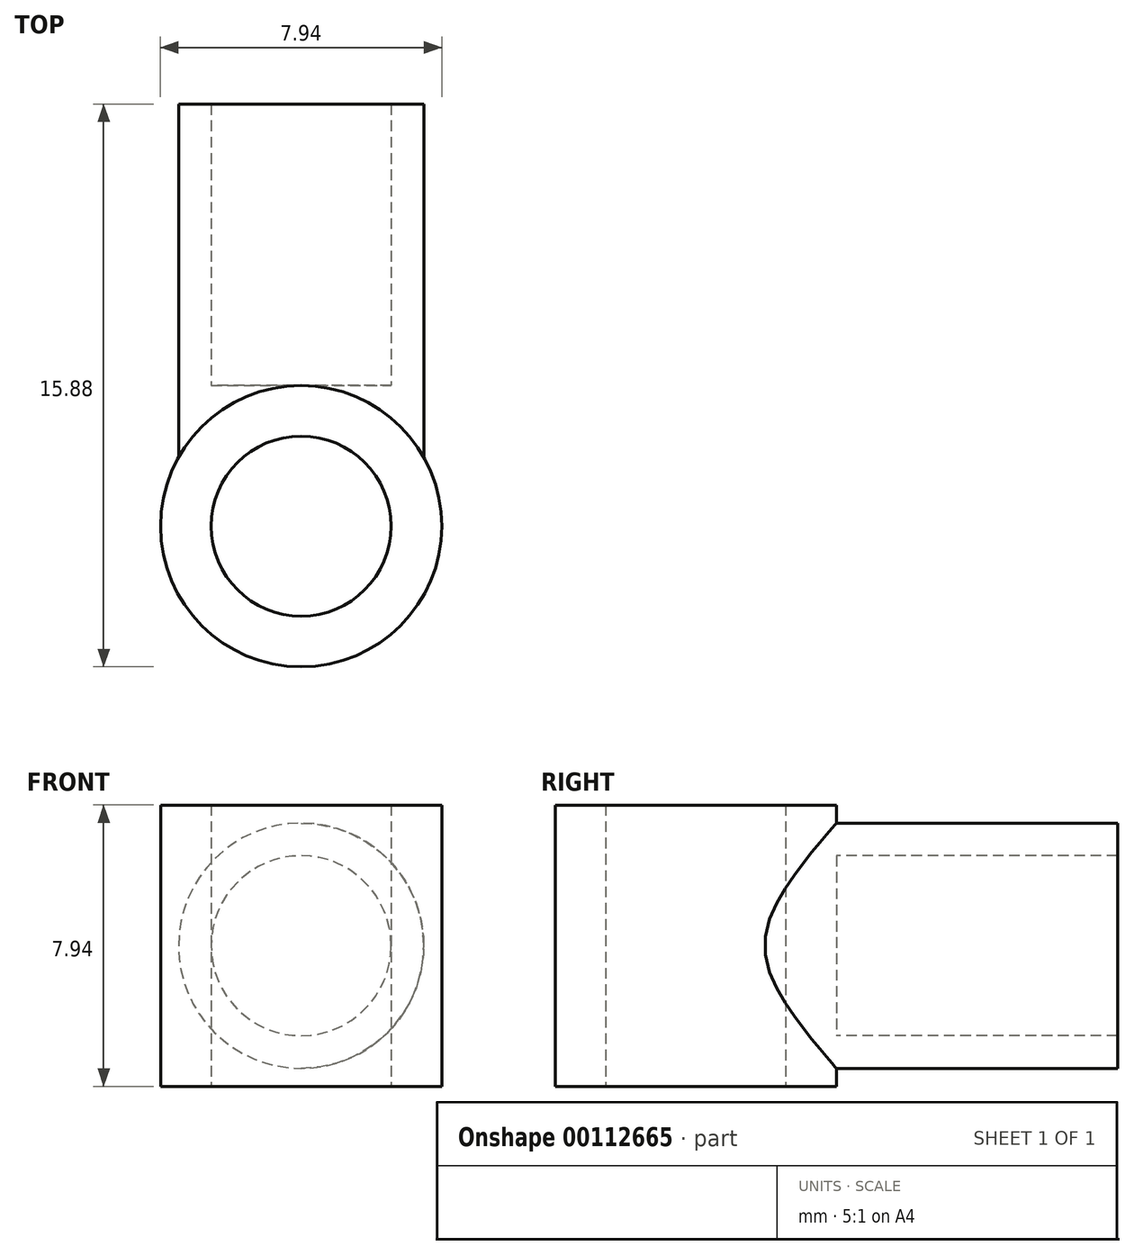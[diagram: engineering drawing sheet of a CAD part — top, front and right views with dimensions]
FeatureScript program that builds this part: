
annotation { "Feature Type Name" : "Feature", "Feature Type Description" : "" }
export const myFeature = defineFeature(function(context is Context, id is Id, definition is map)
    precondition{}
    {
        {
            var Q0;
            Q0=qCreatedBy(makeId("Top.planeOp"),FACE);
            var sketch = newSketch(context, id + "F0", { "sketchPlane" : qUnion([Q0])});
            skLineSegment(sketch, "E0.bottom", {"start": v(3.97, 3.97) * mm, "end": v(-3.97, 3.97) * mm});
            skLineSegment(sketch, "E0.top", {"start": v(3.97, -3.97) * mm, "end": v(-3.97, -3.97) * mm});
            skLineSegment(sketch, "E0.left", {"start": v(3.97, 3.97) * mm, "end": v(3.97, -3.97) * mm});
            skLineSegment(sketch, "E0.right", {"start": v(-3.97, 3.97) * mm, "end": v(-3.97, -3.97) * mm});
            skPoint(sketch, "E0.middle", {"position": v(0, 0) * mm});
            skCircle(sketch, "E1", {"center": v(0, 0) * mm, "radius": 2.54 * mm});
            skSolve(sketch);
        }
        {
            var Q0;
            Q0 = qSketchRegion(id + "F0", true);
            extrude(context, id + "F1", {"entities" : qUnion([Q0]), "depth" : 7.94 * mm});
        }
        {
            var Q0;
            Q0=makeQuery(id+"F1.opExtrude","SWEPT_FACE",FACE,{"disambiguationData":[OSD([sQuery(id+"F0.wireOp",EDGE,"E0.bottom")])]});
            var sketch = newSketch(context, id + "F2", { "sketchPlane" : qUnion([Q0])});
            skLineSegment(sketch, "E2", {"start": v(3.97, 3.97) * mm, "end": v(-3.97, 3.97) * mm, "construction": true});
            skCircle(sketch, "E3", {"center": v(0, 3.97) * mm, "radius": 2.54 * mm});
            skCircle(sketch, "E4", {"center": v(0, 3.97) * mm, "radius": 3.46 * mm});
            skSolve(sketch);
        }
        {
            var Q0;
            Q0 = qSketchRegion(id + "F2", true);
            extrude(context, id + "F3", {"entities" : qUnion([Q0]), "operationType" : NewBodyOperationType.ADD, "depth" : 7.94 * mm});
        }
        {
            var Q0;
            Q0=makeQuery(id+"F1.opExtrude","SWEPT_EDGE",EDGE,{"disambiguationData":[OSD([sQuery(id+"F0.wireOp",EDGE,"E0.bottom"),sQuery(id+"F0.wireOp",EDGE,"E0.right")])]});
            var Q1;
            Q1=makeQuery(id+"F1.opExtrude","SWEPT_EDGE",EDGE,{"disambiguationData":[OSD([sQuery(id+"F0.wireOp",EDGE,"E0.bottom"),sQuery(id+"F0.wireOp",EDGE,"E0.left")])]});
            var Q2;
            Q2=makeQuery(id+"F1.opExtrude","SWEPT_EDGE",EDGE,{"disambiguationData":[OSD([sQuery(id+"F0.wireOp",EDGE,"E0.top"),sQuery(id+"F0.wireOp",EDGE,"E0.left")])]});
            var Q3;
            Q3=makeQuery(id+"F1.opExtrude","SWEPT_EDGE",EDGE,{"disambiguationData":[OSD([sQuery(id+"F0.wireOp",EDGE,"E0.top"),sQuery(id+"F0.wireOp",EDGE,"E0.right")])]});
            fillet(context, id + "F4", {"entities" : qUnion([Q0, Q1, Q2, Q3]), "radius" : 3.97 * mm, "tangentPropagation" : true, "allowEdgeOverflow" : false});
        }
    });
